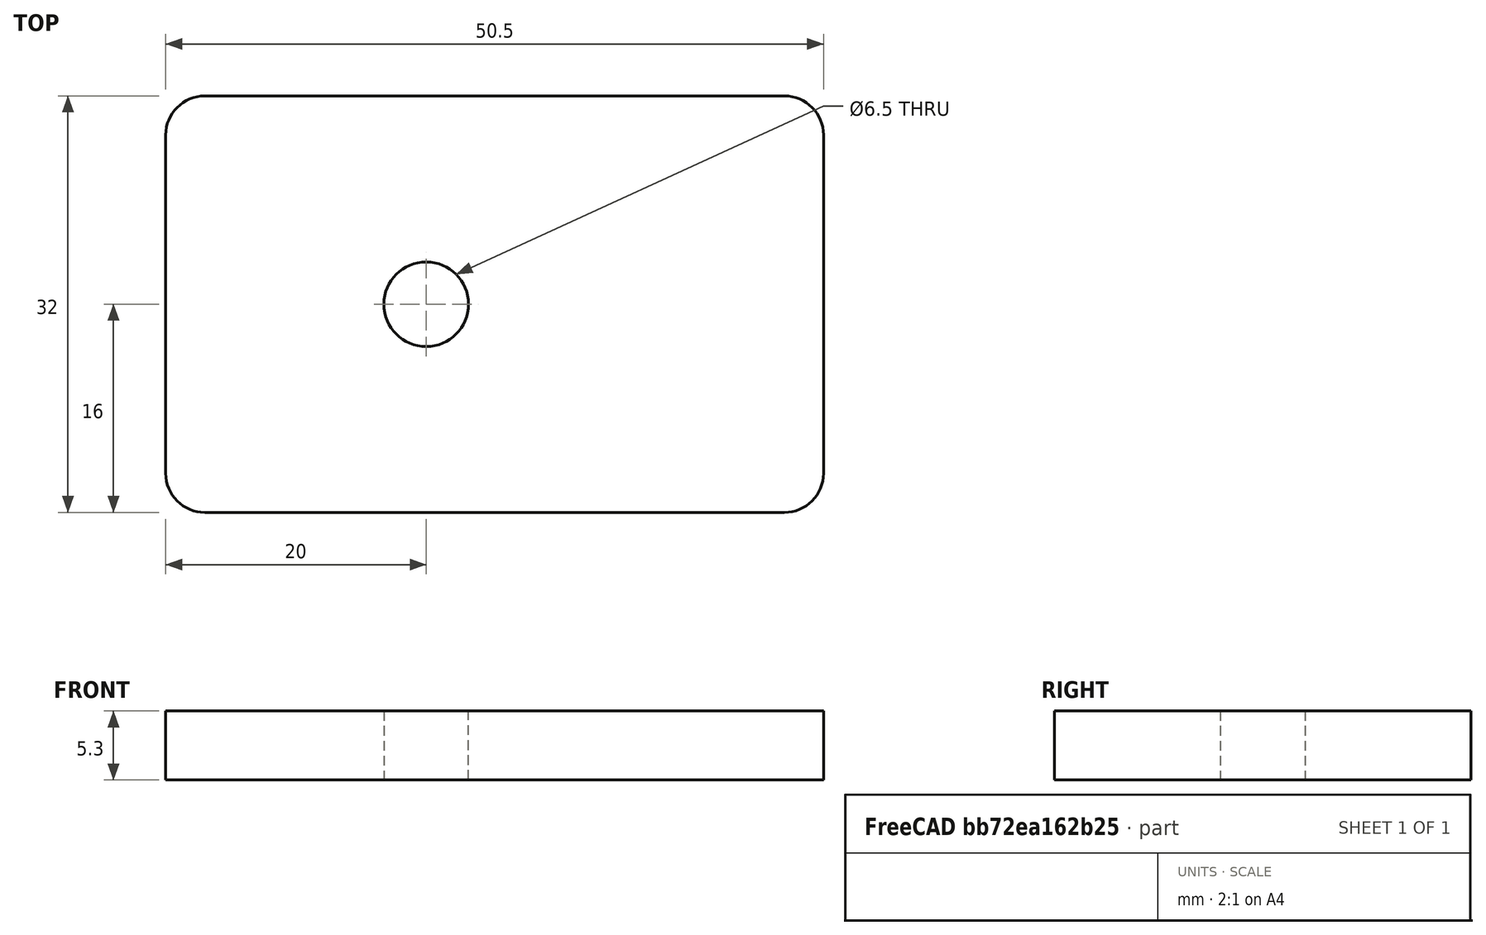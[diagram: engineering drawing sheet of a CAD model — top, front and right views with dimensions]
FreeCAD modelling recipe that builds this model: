
FCSTD DOCUMENT  (FreeCAD 0.19R)
Label: len_mt_pad
License: All rights reserved
LicenseURL: http://en.wikipedia.org/wiki/All_rights_reserved
objects: Sketcher::SketchObject×1, PartDesign::Pad×1, PartDesign::Body×1
note: 4 computed .brp shape members not serialized (recipe doc carries the construction recipe); baked Part::Feature solids carry a one-line shape summary decoded from their .brp

FEATURE [Sketcher::SketchObject] Sketch
  FullyConstrained = true
  MapMode = 5
  Support = -> [XY_Plane]
  expr: Constraints[19] = 50.5 / 2
  sketch-geometry (9):
    g0: LineSegment StartX=-22.25 StartY=16 StartZ=0 EndX=22.25 EndY=16 EndZ=0
    g1: LineSegment StartX=25.25 StartY=13 StartZ=0 EndX=25.25 EndY=-13 EndZ=0
    g2: LineSegment StartX=22.25 StartY=-16 StartZ=0 EndX=-22.25 EndY=-16 EndZ=0
    g3: LineSegment StartX=-25.25 StartY=-13 StartZ=0 EndX=-25.25 EndY=13 EndZ=0
    g4: Circle CenterX=-5.25 CenterY=0 CenterZ=0 NormalX=0 NormalY=0 NormalZ=1 AngleXU=0 Radius=3.25
    g5: ArcOfCircle CenterX=-22.25 CenterY=13 CenterZ=0 NormalX=0 NormalY=0 NormalZ=1 AngleXU=0 Radius=3 StartAngle=1.5708 EndAngle=3.14159
    g6: ArcOfCircle CenterX=22.25 CenterY=13 CenterZ=0 NormalX=0 NormalY=0 NormalZ=1 AngleXU=0 Radius=3 StartAngle=0 EndAngle=1.5708
    g7: ArcOfCircle CenterX=-22.25 CenterY=-13 CenterZ=0 NormalX=0 NormalY=0 NormalZ=1 AngleXU=0 Radius=3 StartAngle=3.14159 EndAngle=4.71239
    g8: ArcOfCircle CenterX=22.25 CenterY=-13 CenterZ=0 NormalX=0 NormalY=0 NormalZ=1 AngleXU=0 Radius=3 StartAngle=4.71239 EndAngle=6.28319
  constraints (23):
    c: Horizontal(g0)
    c: Horizontal(g2)
    c: Vertical(g1)
    c: Vertical(g3)
    c: PointOnObject(g4,g-1)
    c: Diameter(g4) = 6.5
    c: Tangent(g3,g5) = 1.5708
    c: Tangent(g0,g5) = 1.5708
    c: Tangent(g0,g6) = 1.5708
    c: Tangent(g1,g6) = 1.5708
    c: Tangent(g2,g7) = 1.5708
    c: Tangent(g3,g7) = 1.5708
    c: Tangent(g2,g8) = 1.5708
    c: Tangent(g1,g8) = 1.5708
    c: Equal(g5,g6)
    c: Equal(g6,g8)
    c: Equal(g8,g7)
    c: Radius(g6) = 3
    c: DistanceX(g3,g1) = 50.5
    c: DistanceX(g3,g-1) = 25.25
    c: DistanceY(g2,g0) = 32
    c: DistanceY(g-1,g0) = 16
    c: DistanceX(g3,g4) = 20
FEATURE [PartDesign::Pad] Pad
  Direction = (1,1,1)
  Length = 5.3
  Length2 = 100
  Profile = -> Sketch
  Type = 0
FEATURE [PartDesign::Body] Body
  Group = -> [Sketch,Pad]
  Origin = -> Origin
  Tip = -> Pad
